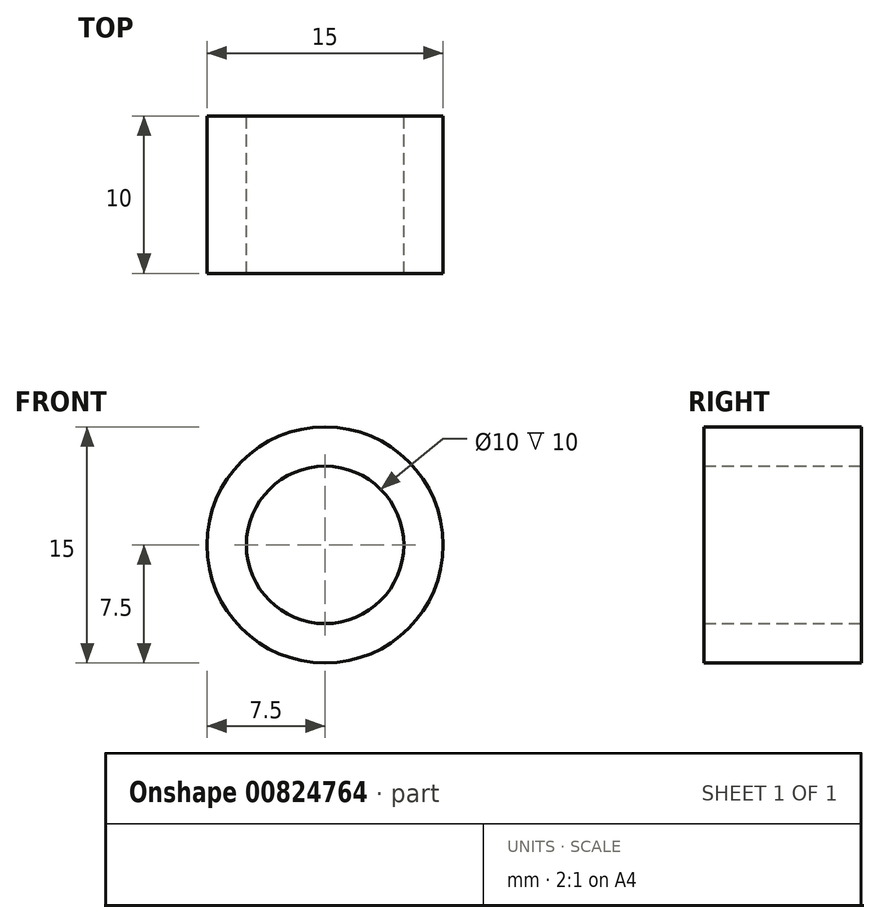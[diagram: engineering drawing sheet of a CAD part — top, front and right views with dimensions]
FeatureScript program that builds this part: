
annotation { "Feature Type Name" : "Feature", "Feature Type Description" : "" }
export const myFeature = defineFeature(function(context is Context, id is Id, definition is map)
    precondition{}
    {
        {
            var Q0;
            Q0=qCreatedBy(makeId("Front.planeOp"),FACE);
            var sketch = newSketch(context, id + "F0", { "sketchPlane" : qUnion([Q0])});
            skCircle(sketch, "E0", {"center": v(0, 0) * mm, "radius": 7.5 * mm});
            skCircle(sketch, "E1", {"center": v(0, 0) * mm, "radius": 5 * mm});
            skSolve(sketch);
        }
        {
            var Q0;
            Q0=makeQuery(id+"F0.imprint","IMPRINT",FACE,{"disambiguationData":[TD([[makeQuery(id+"F0.imprint","IMPRINT",EDGE,{"derivedFrom":sQuery(id+"F0.wireOp",EDGE,"E0")}),1.0]])]});
            extrude(context, id + "F1", {"entities" : qUnion([Q0]), "depth" : 10 * mm, "offsetDistance" : 25 * mm});
        }
    });
